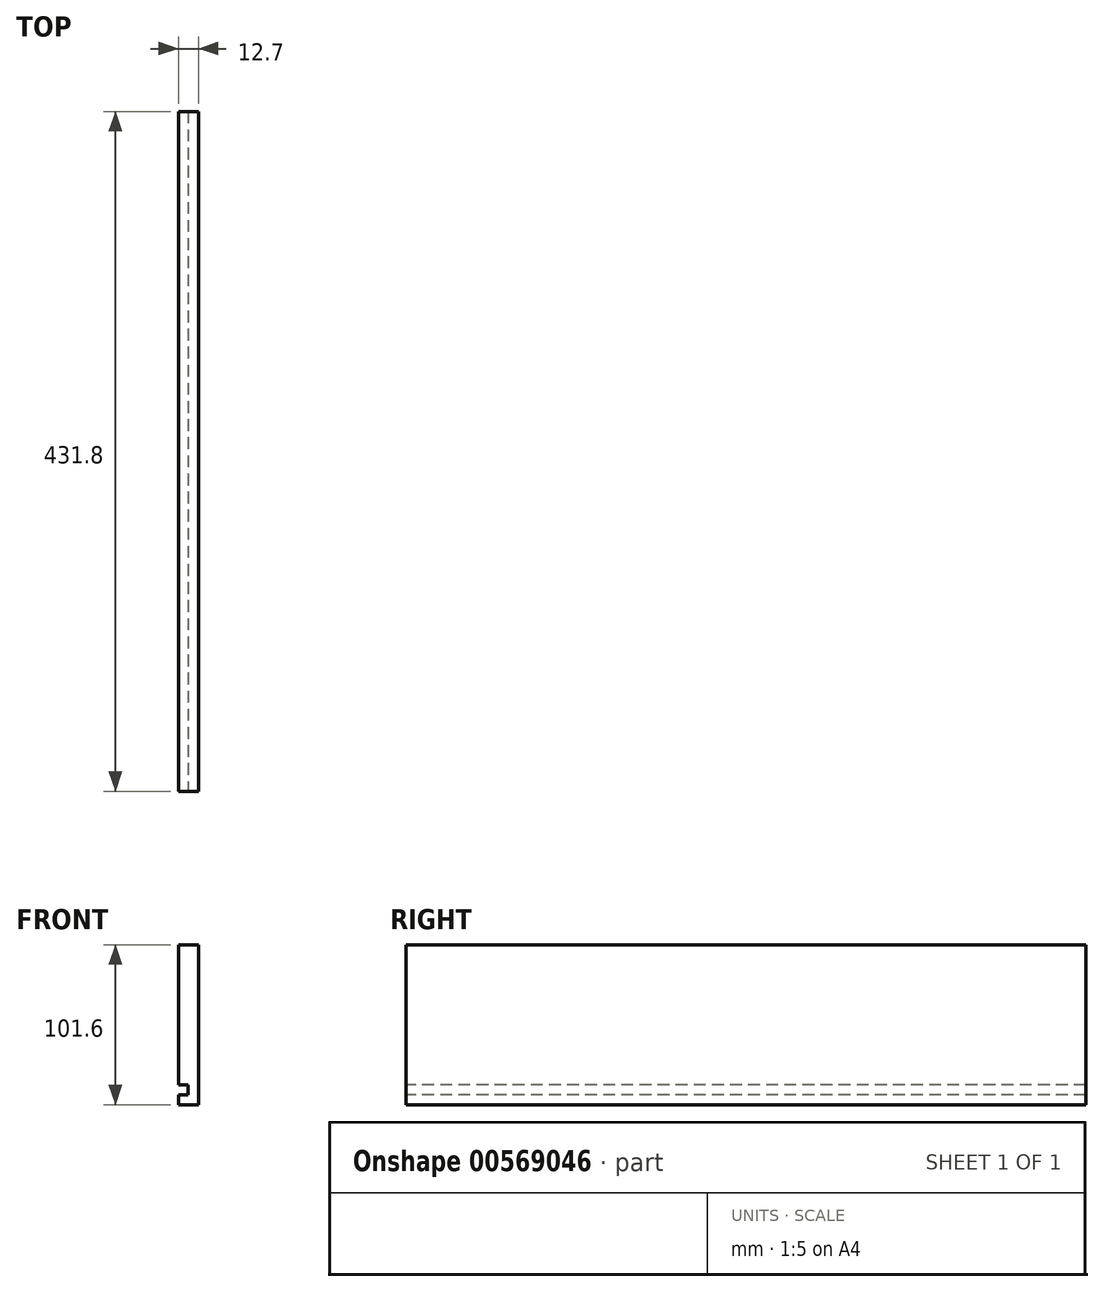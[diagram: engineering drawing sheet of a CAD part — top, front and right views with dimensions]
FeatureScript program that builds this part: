
annotation { "Feature Type Name" : "Feature", "Feature Type Description" : "" }
export const myFeature = defineFeature(function(context is Context, id is Id, definition is map)
    precondition{}
    {
        {
            var Q0;
            Q0=qCreatedBy(makeId("Right.planeOp"),FACE);
            var sketch = newSketch(context, id + "F0", { "sketchPlane" : qUnion([Q0])});
            skLineSegment(sketch, "E0.bottom", {"start": v(-215.9, 50.8) * mm, "end": v(215.9, 50.8) * mm});
            skLineSegment(sketch, "E0.top", {"start": v(-215.9, -50.8) * mm, "end": v(215.9, -50.8) * mm});
            skLineSegment(sketch, "E0.left", {"start": v(-215.9, 50.8) * mm, "end": v(-215.9, -50.8) * mm});
            skLineSegment(sketch, "E0.right", {"start": v(215.9, 50.8) * mm, "end": v(215.9, -50.8) * mm});
            skPoint(sketch, "E0.middle", {"position": v(0, 0) * mm});
            skSolve(sketch);
        }
        {
            var Q0;
            Q0 = qSketchRegion(id + "F0", true);
            extrude(context, id + "F1", {"entities" : qUnion([Q0]), "endBound" : BoundingType.SYMMETRIC, "depth" : 12.7 * mm, "offsetDistance" : 25.4 * mm});
        }
        {
            var Q0;
            Q0=qCreatedBy(makeId("Front.planeOp"),FACE);
            var sketch = newSketch(context, id + "F2", { "sketchPlane" : qUnion([Q0])});
            skLineSegment(sketch, "E1.0", {"start": v(-6.35, 50.8) * mm, "end": v(-6.35, -50.8) * mm});
            skLineSegment(sketch, "E2.0", {"start": v(6.35, -50.8) * mm, "end": v(-6.35, -50.8) * mm});
            skLineSegment(sketch, "E3.bottom", {"start": v(-6.35, -38.1) * mm, "end": v(0, -38.1) * mm});
            skLineSegment(sketch, "E3.top", {"start": v(-6.35, -44.45) * mm, "end": v(0, -44.45) * mm});
            skLineSegment(sketch, "E3.left", {"start": v(-6.35, -38.1) * mm, "end": v(-6.35, -44.45) * mm});
            skLineSegment(sketch, "E3.right", {"start": v(0, -38.1) * mm, "end": v(0, -44.45) * mm});
            skSolve(sketch);
        }
        {
            var Q0;
            Q0 = qSketchRegion(id + "F2", true);
            extrude(context, id + "F3", {"entities" : qUnion([Q0]), "operationType" : NewBodyOperationType.REMOVE, "endBound" : BoundingType.THROUGH_ALL, "oppositeDirection" : true, "depth" : 25.4 * mm, "offsetDistance" : 25.4 * mm, "hasSecondDirection" : true, "secondDirectionBound" : SecondDirectionBoundingType.THROUGH_ALL, "secondDirectionOppositeDirection" : false, "secondDirectionDepth" : 25.4 * mm});
        }
    });
